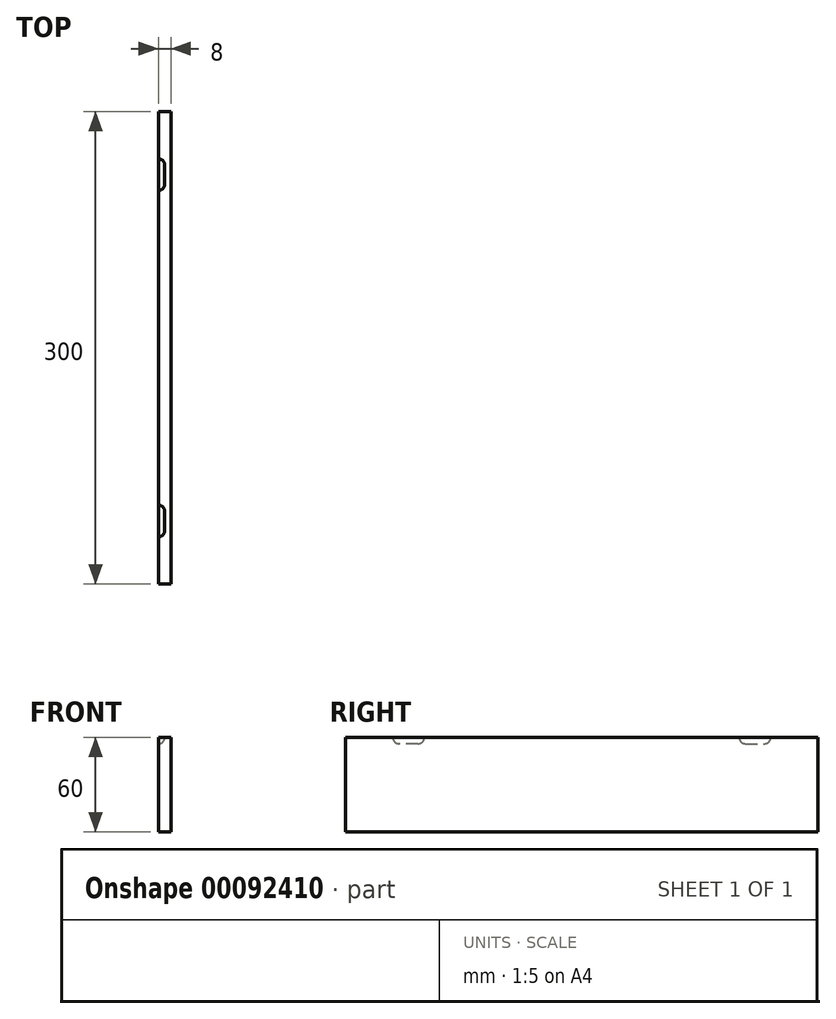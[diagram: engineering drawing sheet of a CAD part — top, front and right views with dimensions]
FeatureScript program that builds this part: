
annotation { "Feature Type Name" : "Feature", "Feature Type Description" : "" }
export const myFeature = defineFeature(function(context is Context, id is Id, definition is map)
    precondition{}
    {
        {
            var Q0;
            Q0=qCreatedBy(makeId("Front.planeOp"),FACE);
            var sketch = newSketch(context, id + "F0", { "sketchPlane" : qUnion([Q0])});
            skLineSegment(sketch, "E0.bottom", {"start": v(4, -30) * mm, "end": v(-4, -30) * mm});
            skLineSegment(sketch, "E0.top", {"start": v(4, 30) * mm, "end": v(-4, 30) * mm});
            skLineSegment(sketch, "E0.left", {"start": v(4, -30) * mm, "end": v(4, 30) * mm});
            skLineSegment(sketch, "E0.right", {"start": v(-4, -30) * mm, "end": v(-4, 30) * mm});
            skPoint(sketch, "E0.middle", {"position": v(0, 0) * mm});
            skSolve(sketch);
        }
        {
            var Q0;
            Q0=makeQuery(id+"F0.imprint","IMPRINT",FACE,{"disambiguationData":[TD([[makeQuery(id+"F0.imprint","IMPRINT",EDGE,{"derivedFrom":sQuery(id+"F0.wireOp",EDGE,"E0.bottom")}),-1.0]])]});
            extrude(context, id + "F1", {"entities" : qUnion([Q0]), "endBound" : BoundingType.SYMMETRIC, "depth" : 300 * mm});
        }
        {
            var Q0;
            Q0=qCreatedBy(makeId("Front.planeOp"),FACE);
            cPlane(context, id + "F2", {"entities" : qUnion([Q0]), "cplaneType" : CPlaneType.OFFSET, "offset" : 120 * mm, "width" : 150 * mm, "height" : 150 * mm});
        }
        {
            var Q0;
            Q0=qCreatedBy(id+"F2.planeOp",FACE);
            var sketch = newSketch(context, id + "F3", { "sketchPlane" : qUnion([Q0])});
            skCircle(sketch, "E1", {"center": v(-4, 30) * mm, "radius": 4 * mm});
            skSolve(sketch);
        }
        {
            var Q0;
            Q0=makeQuery(id+"F3.imprint","IMPRINT",FACE,{"disambiguationData":[TD([[makeQuery(id+"F3.imprint","IMPRINT",EDGE,{"derivedFrom":sQuery(id+"F3.wireOp",EDGE,"E1")}),1.0]])]});
            extrude(context, id + "F4", {"entities" : qUnion([Q0]), "oppositeDirection" : true, "depth" : 20 * mm});
        }
        {
            var Q0;
            Q0=makeQuery(id+"F4.opExtrude","CAP_EDGE",EDGE,{"disambiguationData":[OSD([sQuery(id+"F3.wireOp",EDGE,"E1")])],"isStart":true});
            var Q1;
            Q1=makeQuery(id+"F4.opExtrude","CAP_EDGE",EDGE,{"disambiguationData":[OSD([sQuery(id+"F3.wireOp",EDGE,"E1")])],"isStart":false});
            fillet(context, id + "F5", {"entities" : qUnion([Q0, Q1]), "radius" : 4 * mm, "tangentPropagation" : true, "allowEdgeOverflow" : false});
        }
        {
            var Q0;
            Q0=makeQuery(id+"F4.opExtrude","SWEPT_BODY",BODY,{"disambiguationData":[OSD([sQuery(id+"F3.wireOp",EDGE,"E1")])]});
            var Q1;
            Q1=qCreatedBy(makeId("Front.planeOp"),FACE);
            mirror(context, id + "F6", {"entities" : qUnion([Q0]), "mirrorPlane" : qUnion([Q1])});
        }
        {
            var Q0;
            Q0=makeQuery(id+"F6.opPattern","COPY",BODY,{"derivedFrom":makeQuery(id+"F4.opExtrude","SWEPT_BODY",BODY,{"disambiguationData":[OSD([sQuery(id+"F3.wireOp",EDGE,"E1")])]}),"instanceName":"1"});
            var Q1;
            Q1=makeQuery(id+"F4.opExtrude","SWEPT_BODY",BODY,{"disambiguationData":[OSD([sQuery(id+"F3.wireOp",EDGE,"E1")])]});
            var Q2;
            Q2=makeQuery(id+"F1.opExtrude","SWEPT_BODY",BODY,{"disambiguationData":[OSD([sQuery(id+"F0.wireOp",EDGE,"E0.bottom"),sQuery(id+"F0.wireOp",EDGE,"E0.top"),sQuery(id+"F0.wireOp",EDGE,"E0.left"),sQuery(id+"F0.wireOp",EDGE,"E0.right")])]});
            booleanBodies(context, id + "F7", {"operationType" : BooleanOperationType.SUBTRACTION, "tools" : qUnion([Q0, Q1]), "targets" : qUnion([Q2])});
        }
    });
